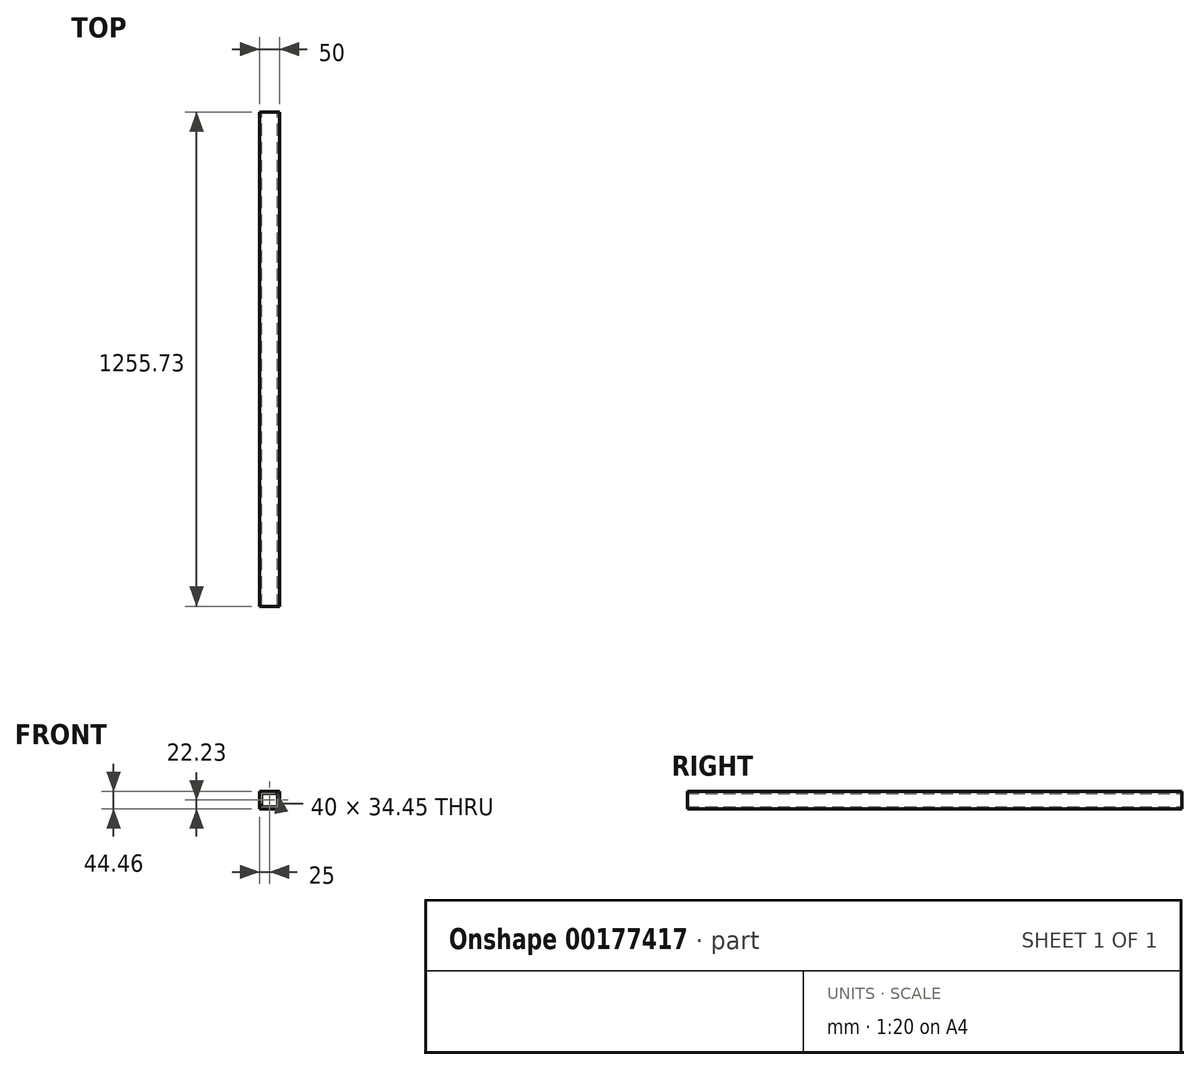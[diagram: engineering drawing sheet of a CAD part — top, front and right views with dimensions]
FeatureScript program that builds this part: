
annotation { "Feature Type Name" : "Feature", "Feature Type Description" : "" }
export const myFeature = defineFeature(function(context is Context, id is Id, definition is map)
    precondition{}
    {
        {
            var Q0;
            Q0=qCreatedBy(makeId("Front.planeOp"),FACE);
            var sketch = newSketch(context, id + "F0", { "sketchPlane" : qUnion([Q0])});
            skLineSegment(sketch, "E0.bottom", {"start": v(25, -22.22) * mm, "end": v(-25, -22.23) * mm});
            skLineSegment(sketch, "E0.top", {"start": v(25, 22.23) * mm, "end": v(-25, 22.23) * mm});
            skLineSegment(sketch, "E0.left", {"start": v(25, -22.22) * mm, "end": v(25, 22.23) * mm});
            skLineSegment(sketch, "E0.right", {"start": v(-25, -22.23) * mm, "end": v(-25, 22.22) * mm});
            skPoint(sketch, "E0.middle", {"position": v(0, 0) * mm});
            skLineSegment(sketch, "E1.0", {"start": v(20, 17.22) * mm, "end": v(-20, 17.22) * mm});
            skLineSegment(sketch, "E1.1", {"start": v(20, -17.22) * mm, "end": v(20, 17.22) * mm});
            skLineSegment(sketch, "E1.2", {"start": v(20, -17.22) * mm, "end": v(-20, -17.22) * mm});
            skLineSegment(sketch, "E1.3", {"start": v(-20, -17.22) * mm, "end": v(-20, 17.22) * mm});
            skSolve(sketch);
        }
        {
            var Q0;
            Q0=makeQuery(id+"F0.imprint","IMPRINT",FACE,{"disambiguationData":[TD([[makeQuery(id+"F0.imprint","IMPRINT",EDGE,{"derivedFrom":sQuery(id+"F0.wireOp",EDGE,"E0.bottom")}),-1.0]])]});
            extrude(context, id + "F1", {"entities" : qUnion([Q0]), "depth" : 1255.73 * mm});
        }
    });
